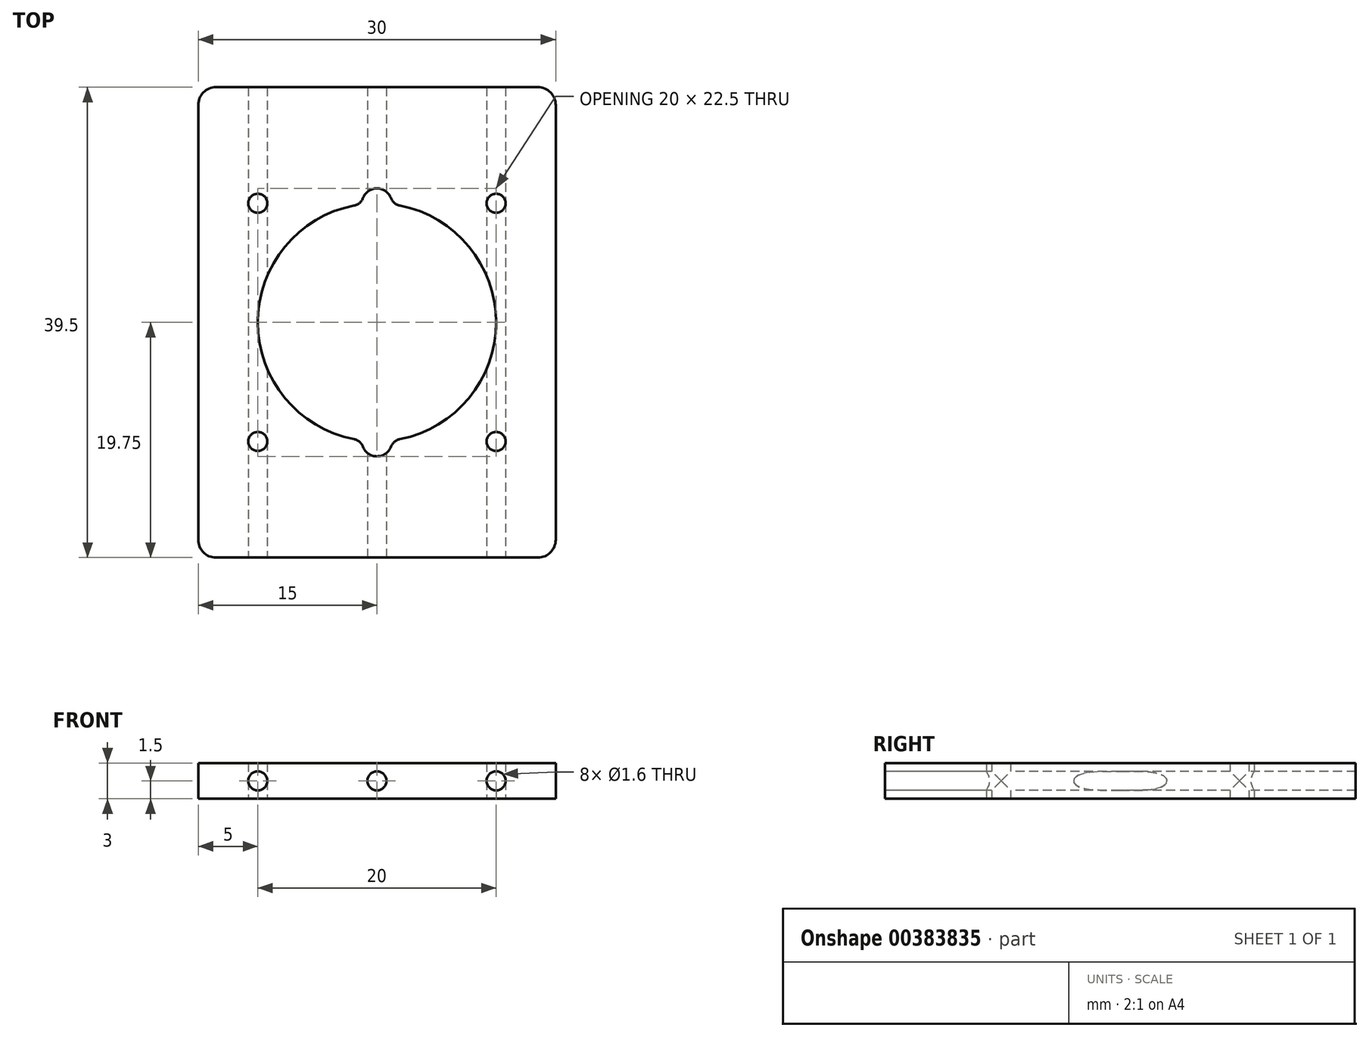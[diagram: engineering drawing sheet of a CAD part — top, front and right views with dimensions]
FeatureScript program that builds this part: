
annotation { "Feature Type Name" : "Feature", "Feature Type Description" : "" }
export const myFeature = defineFeature(function(context is Context, id is Id, definition is map)
    precondition{}
    {
        {
            var Q0;
            Q0=qCreatedBy(makeId("Top.planeOp"),FACE);
            var sketch = newSketch(context, id + "F0", { "sketchPlane" : qUnion([Q0])});
            skLineSegment(sketch, "E0.bottom", {"start": v(-13.5, 19.75) * mm, "end": v(13.5, 19.75) * mm});
            skLineSegment(sketch, "E0.top", {"start": v(-13.5, -19.75) * mm, "end": v(13.5, -19.75) * mm});
            skLineSegment(sketch, "E0.left", {"start": v(-15, 18.25) * mm, "end": v(-15, -18.25) * mm});
            skLineSegment(sketch, "E0.right", {"start": v(15, 18.25) * mm, "end": v(15, -18.25) * mm});
            skPoint(sketch, "E0.middle", {"position": v(0, 0) * mm});
            skLineSegment(sketch, "E1.bottom", {"start": v(-10, 10) * mm, "end": v(10, 10) * mm, "construction": true});
            skLineSegment(sketch, "E1.top", {"start": v(-10, -10) * mm, "end": v(10, -10) * mm, "construction": true});
            skLineSegment(sketch, "E1.left", {"start": v(-10, 10) * mm, "end": v(-10, -10) * mm, "construction": true});
            skLineSegment(sketch, "E1.right", {"start": v(10, 10) * mm, "end": v(10, -10) * mm, "construction": true});
            skCircle(sketch, "E2", {"center": v(-10, 10) * mm, "radius": 0.8 * mm});
            skCircle(sketch, "E3.1.0", {"center": v(-10, -10) * mm, "radius": 0.8 * mm});
            skCircle(sketch, "E3.2.0", {"center": v(10, -10) * mm, "radius": 0.8 * mm});
            skCircle(sketch, "E4.1.3.0", {"center": v(10, 10) * mm, "radius": 0.8 * mm});
            skLineSegment(sketch, "E5", {"start": v(0, 19.75) * mm, "end": v(0, 10) * mm, "construction": true});
            skLineSegment(sketch, "E6", {"start": v(-10, 19.75) * mm, "end": v(-10, 10) * mm, "construction": true});
            skPoint(sketch, "E7.visualSharp", {"position": v(-15, 19.75) * mm});
            skArc(sketch, "E7.filletArc", {"start": v(-13.5, 19.75) * mm, "mid": v(-14.56, 19.31) * mm, "end": v(-15, 18.25) * mm});
            skPoint(sketch, "E8.visualSharp", {"position": v(15, 19.75) * mm});
            skArc(sketch, "E8.filletArc", {"start": v(15, 18.25) * mm, "mid": v(14.56, 19.31) * mm, "end": v(13.5, 19.75) * mm});
            skPoint(sketch, "E9.visualSharp", {"position": v(15, -19.75) * mm});
            skArc(sketch, "E9.filletArc", {"start": v(13.5, -19.75) * mm, "mid": v(14.56, -19.31) * mm, "end": v(15, -18.25) * mm});
            skPoint(sketch, "E10.visualSharp", {"position": v(-15, -19.75) * mm});
            skArc(sketch, "E10.filletArc", {"start": v(-15, -18.25) * mm, "mid": v(-14.56, -19.31) * mm, "end": v(-13.5, -19.75) * mm});
            skPoint(sketch, "E11", {"position": v(-10, 10.8) * mm});
            skCircle(sketch, "E12", {"center": v(0, 0) * mm, "radius": 10 * mm});
            skArc(sketch, "E13", {"start": v(1.25, 10) * mm, "mid": v(0, 11.25) * mm, "end": v(-1.25, 10) * mm});
            skLineSegment(sketch, "E14", {"start": v(-1.25, 10) * mm, "end": v(-1.25, 9.92) * mm});
            skLineSegment(sketch, "E15.MirrorCS", {"start": v(1.25, 10) * mm, "end": v(1.25, 9.92) * mm});
            skLineSegment(sketch, "E16.MirrorCS", {"start": v(-1.25, -10) * mm, "end": v(-1.25, -9.92) * mm});
            skLineSegment(sketch, "E17.MirrorCS", {"start": v(1.25, -10) * mm, "end": v(1.25, -9.92) * mm});
            skArc(sketch, "E18.MirrorCS", {"start": v(1.25, -10) * mm, "mid": v(0, -11.25) * mm, "end": v(-1.25, -10) * mm});
            skSolve(sketch);
        }
        {
            var Q0;
            Q0=qSketchRegion(id+"F0",true);
            extrude(context, id + "F1", {"entities" : qUnion([Q0]), "depth" : 3 * mm, "offsetDistance" : 25 * mm});
        }
        {
            var Q0;
            Q0=makeQuery(id+"F1.opExtrude","SWEPT_FACE",FACE,{"disambiguationData":[OSD([sQuery(id+"F0.wireOp",EDGE,"E0.top")])]});
            var sketch = newSketch(context, id + "F2", { "sketchPlane" : qUnion([Q0])});
            skLineSegment(sketch, "E19", {"start": v(0, 3) * mm, "end": v(0, 0) * mm, "construction": true});
            skCircle(sketch, "E20", {"center": v(0, 1.5) * mm, "radius": 0.8 * mm});
            skCircle(sketch, "E21", {"center": v(10, 1.5) * mm, "radius": 0.8 * mm});
            skCircle(sketch, "E22.MirrorC", {"center": v(-10, 1.5) * mm, "radius": 0.8 * mm});
            skSolve(sketch);
        }
        {
            var Q0;
            Q0=qSketchRegion(id+"F2",true);
            extrude(context, id + "F3", {"entities" : qUnion([Q0]), "operationType" : NewBodyOperationType.REMOVE, "endBound" : BoundingType.THROUGH_ALL, "oppositeDirection" : true, "depth" : 25 * mm, "offsetDistance" : 25 * mm});
        }
        {
            var Q0;
            Q0=makeQuery(id+"F1.opExtrude","SWEPT_EDGE",EDGE,{"disambiguationData":[OSD([sQuery(id+"F0.wireOp",EDGE,"E12"),sQuery(id+"F0.wireOp",EDGE,"E15.MirrorCS")])]});
            var Q1;
            Q1=makeQuery(id+"F1.opExtrude","SWEPT_EDGE",EDGE,{"disambiguationData":[OSD([sQuery(id+"F0.wireOp",EDGE,"E12"),sQuery(id+"F0.wireOp",EDGE,"E14")])]});
            var Q2;
            Q2=makeQuery(id+"F1.opExtrude","SWEPT_EDGE",EDGE,{"disambiguationData":[OSD([sQuery(id+"F0.wireOp",EDGE,"E12"),sQuery(id+"F0.wireOp",EDGE,"E16.MirrorCS")])]});
            var Q3;
            Q3=makeQuery(id+"F1.opExtrude","SWEPT_EDGE",EDGE,{"disambiguationData":[OSD([sQuery(id+"F0.wireOp",EDGE,"E12"),sQuery(id+"F0.wireOp",EDGE,"E17.MirrorCS")])]});
            fillet(context, id + "F4", {"entities" : qUnion([Q0, Q1, Q2, Q3]), "radius" : 1 * mm, "tangentPropagation" : true, "allowEdgeOverflow" : false});
        }
    });
